# Revit family: FU_Stool_Sandler_Palm Beach 3-2
name_source: partatom
category: Furniture
units: mm (PartAtom-declared; Revit-internal decimal feet)

## family parameters
Always vertical = Yes
Cut with Voids When Loaded = No
OmniClass Number = 23.40.20.00
OmniClass Title = General Furniture and Specialties
Room Calculation Point = No
Shared = No
Work Plane-Based = No

## types (1)
- Palm Beach 3.2
    Default Elevation = 0 mm  [stored 0 ft]
    Depth = 530 mm  [stored 1.73885 ft]
    Description = Barstool with solid beech frame and upholstered back with square button pattern.
With kickplates.
    Frame = Wood - Beech - Dark Cherry
    Height = 1115 mm  [stored 3.65814 ft]
    Manufacturer = Sandler
    Model = Palm Beach 3.2
    Seat = Leather - Sandler 227
    URL = https://www.sandlerseating.com
    Width = 430 mm  [stored 1.41076 ft]

note: [stored X ft] marks values corroborated as IEEE doubles in the binary element streams (Revit-internal decimal feet)

## geometry (parser evidence)
native form markers: Sweep x3
no freeform markers — native parametric forms only
